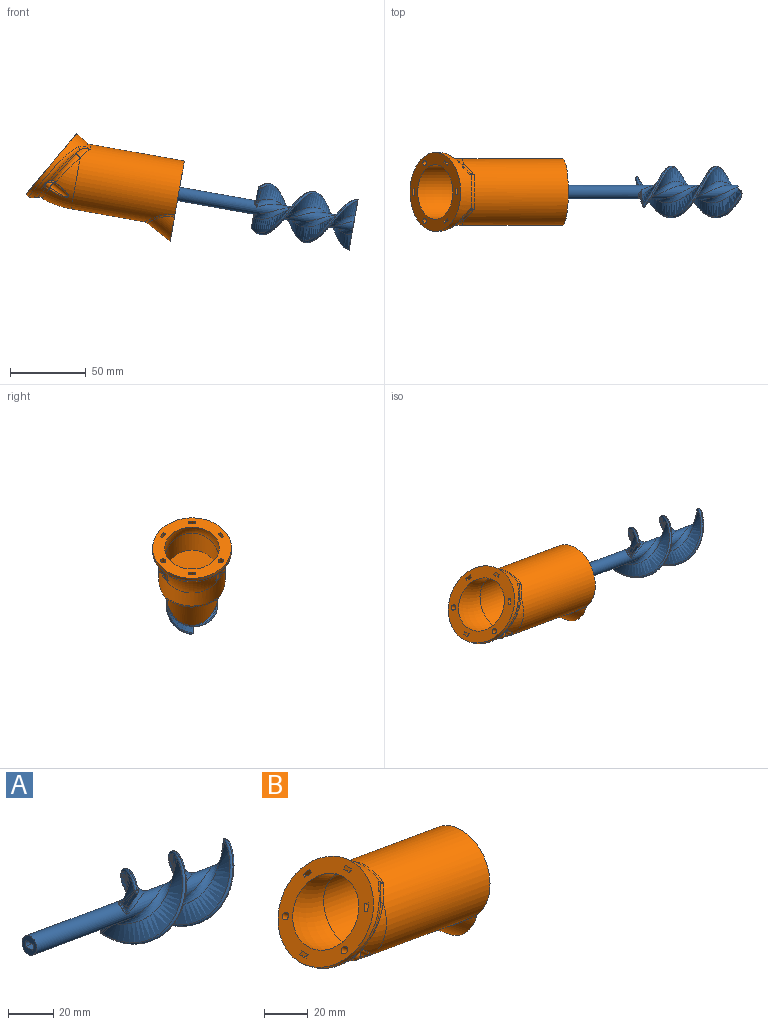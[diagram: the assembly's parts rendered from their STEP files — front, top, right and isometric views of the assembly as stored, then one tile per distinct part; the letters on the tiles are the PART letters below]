
ASSEMBLY  parts=2 mates=1
PART A: 48 faces, bbox 125.7x35.5x45.3 mm
  f0: bspline ~66.49x37.08mm, area 953.6mm2, adj f3,f20,f22,f23
  f1: bspline ~66.17x37.12mm, area 953.6mm2, adj f3,f19,f34,f35
  f2: plane 9.56x6.22mm, normal (-0.98,0,0.17), area 10.2mm2, adj f34,f36,f39,f41,f44,f45
  f3: plane 34.01x9.52mm, normal (0.98,0,-0.17), area 165.7mm2, adj f0,f1,f4,f5,f6,f7,f9,f11
  f4: bspline ~64.6x36.57mm, area 928.2mm2, adj f3,f18,f40,f44
  f5: bspline ~66.7x39.44mm, area 7mm2, adj f3,f35,f39,f40
  f6: bspline ~65.33x36.97mm, area 928.2mm2, adj f3,f21,f28,f32
  f7: bspline ~68.93x40.1mm, area 7mm2, adj f3,f23,f27,f28
  f8: plane 9.56x6.22mm, normal (-0.98,0,0.17), area 10.2mm2, adj f22,f24,f27,f29,f32,f33
  f9: cylinder r=4.5mm len=52.09mm, axis (0.98,0,-0.17), area 266.9mm2, adj f3,f10,f18,f20
  f10: cylinder r=4.5mm len=113.15mm, axis (0.98,0,-0.17), area 2007.6mm2, adj f9,f11,f12,f18,f19,f20,f21,f26
  f11: cylinder r=4.5mm len=22.25mm, axis (0.98,0,-0.17), area 89.1mm2, adj f3,f10,f19,f21
  f12: plane 9x8.86mm, normal (-0.98,0,0.17), area 49.6mm2, adj f10,f13,f14,f15,f16
  f13: plane 5.91x4mm, normal (-0.17,0,-0.98), area 24mm2, adj f12,f14,f16,f17
  f14: cylinder r=2.5mm len=6.43mm, axis (-0.98,0,0.17), area 19.3mm2, adj f12,f13,f15,f17
  f15: plane 5.91x4mm, normal (0.17,0,0.98), area 24mm2, adj f12,f14,f16,f17
  f16: cylinder r=2.5mm len=6.43mm, axis (-0.98,0,0.17), area 19.3mm2, adj f12,f13,f15,f17
  f17: plane 5x2.95mm, normal (-0.98,0,0.17), area 14mm2, adj f13,f14,f15,f16
  f18: bspline ~68.92x18.41mm, area 297.1mm2, adj f3,f4,f9,f10,f45
  f19: bspline ~70.5x19.33mm, area 299.9mm2, adj f1,f3,f10,f11,f36
  f20: bspline ~70.9x19.32mm, area 299.9mm2, adj f0,f3,f9,f10,f24
  f21: bspline ~69.05x19.32mm, area 297.1mm2, adj f3,f6,f10,f11,f33
  f22: bspline ~11.42x8.54mm, area 6.7mm2, adj f0,f8,f24,f25
  f23: bspline ~67.36x39.06mm, area 200.2mm2, adj f0,f3,f7,f25
  f24: bspline ~5.09x3.68mm, area 3.4mm2, adj f8,f20,f22,f26
  f25: sphere r=1mm, area 0.5mm2, adj f22,f23,f27
  f26: bspline ~3.52x1.96mm, area 1.9mm2, adj f10,f24,f29
  f27: bspline ~1.47x1.41mm, area 0.1mm2, adj f7,f8,f25,f30
  f28: bspline ~66.17x39.06mm, area 197.7mm2, adj f3,f6,f7,f30
  f29: torus R=5.5mm, axis (0.98,0,-0.17), area 2.8mm2, adj f8,f10,f26,f31
  f30: sphere r=1mm, area 1.5mm2, adj f27,f28,f32
  f31: bspline ~3.9x1.82mm, area 1.9mm2, adj f10,f29,f33
  f32: bspline ~12.63x9.51mm, area 22.6mm2, adj f6,f8,f30,f33
  f33: bspline ~6.38x2.81mm, area 5.7mm2, adj f8,f21,f31,f32
  f34: bspline ~11.46x8.54mm, area 6.7mm2, adj f1,f2,f36,f37
  f35: bspline ~66.3x39.14mm, area 200.2mm2, adj f1,f3,f5,f37
  f36: bspline ~5.09x3.82mm, area 3.4mm2, adj f2,f19,f34,f38
  f37: sphere r=1mm, area 0.7mm2, adj f34,f35,f39
  f38: bspline ~3.8x1.99mm, area 1.9mm2, adj f10,f36,f41
  f39: bspline ~1.58x1.47mm, area 0.1mm2, adj f2,f5,f37,f42
  f40: bspline ~65.33x38.94mm, area 197.7mm2, adj f3,f4,f5,f42
  f41: torus R=5.5mm, axis (0.98,0,-0.17), area 2.8mm2, adj f2,f10,f38,f43
  f42: sphere r=1mm, area 1.4mm2, adj f39,f40,f44
  f43: bspline ~3.32x2.46mm, area 1.9mm2, adj f10,f41,f45
  f44: bspline ~12.77x9.51mm, area 22.6mm2, adj f2,f4,f42,f45
  f45: bspline ~6.17x2.83mm, area 5.7mm2, adj f2,f18,f43,f44
  f46: cone r=0mm half-angle=59deg, axis (0.98,0,-0.17), area 1.3mm2, adj f47
  f47: cylinder r=0.6mm len=15.97mm, axis (0.98,0,-0.17), area 60.3mm2, adj f3,f46
PART B: 95 faces, bbox 123.3x72.3x89.8 mm
  f0: bspline ~21.17x20.89mm, area 78.8mm2, adj f1,f90,f91,f92,f93,f94
  f1: plane 6.16x5.23mm, normal (0.77,0,-0.64), area 19.3mm2, adj f0,f2,f84,f85,f87,f88,f89,f90
  f2: bspline ~2.61x1.99mm, area 2.3mm2, adj f1,f3,f84,f88
  f3: bspline ~4.22x3.01mm, area 3.2mm2, adj f2,f4,f83,f84
  f4: bspline ~3.88x3.69mm, area 3.3mm2, adj f3,f5,f6,f84
  f5: bspline ~4.67x2.25mm, area 3.2mm2, adj f4,f84,f93,f94
  f6: bspline ~52x33.72mm, area 400.3mm2, adj f4,f7,f79,f80,f81,f82,f83,f93
  f7: bspline ~3.69x3.56mm, area 3.3mm2, adj f6,f8,f77,f78
  f8: bspline ~4.22x3.01mm, area 3.2mm2, adj f7,f9,f78,f83
  f9: bspline ~2.97x2.27mm, area 2.3mm2, adj f8,f10,f78,f88
  f10: plane 6.16x5.23mm, normal (0.77,0,-0.64), area 19.3mm2, adj f9,f11,f12,f14,f15,f16,f76,f78
  f11: bspline ~2.77x1.84mm, area 2.1mm2, adj f10,f16,f77,f78
  f12: bspline ~2.37x2.15mm, area 0.7mm2, adj f10,f13,f14,f88
  f13: bspline ~15.13x11.52mm, area 24.5mm2, adj f12,f14,f15,f91
  f14: cylinder r=3mm len=13.01mm, axis (-0.77,0,0.64), area 62.7mm2, adj f10,f12,f13,f15
  f15: bspline ~2.57x2.06mm, area 1mm2, adj f10,f13,f14,f16
  f16: bspline ~21.52x21.22mm, area 78.8mm2, adj f10,f11,f15,f17,f79,f91
  f17: bspline ~11.35x10.37mm, area 31.2mm2, adj f16,f18,f21,f79,f80
  f18: bspline ~2.84x1.97mm, area 0.9mm2, adj f17,f19,f80
  f19: bspline ~27.31x5.39mm, area 48.2mm2, adj f18,f20,f21,f81
  f20: bspline ~2.84x1.97mm, area 0.9mm2, adj f19,f82,f92
  f21: cylinder r=22mm len=74.61mm, axis (-0.98,0,0.17), area 8639.8mm2, adj f17,f19,f22,f24,f91,f92
  f22: bspline ~34.5x21.07mm, area 105.4mm2, adj f21,f23,f24
  f23: extruded ~32.71x11.03mm, area 0mm2, adj f22,f24
  f24: plane 71.91x62.94mm, normal (0.98,0,-0.17), area 1281.1mm2, adj f21,f22,f23,f25,f66,f67,f68,f69
  f25: cylinder r=0.75mm len=4.2mm, axis (-0.98,0,0.17), area 18.8mm2, adj f24,f26
  f26: plane 36x27.12mm, normal (-0.98,0,0.17), area 673.3mm2, adj f25,f27,f28,f33,f37,f60,f65
  f27: torus R=19.9mm, axis (0.98,0,-0.17), area 98.8mm2, adj f26,f28,f65,f73
  f28: bspline ~3.69x3.37mm, area 3.5mm2, adj f26,f27,f29,f33
  f29: bspline ~3.84x2.38mm, area 0mm2, adj f28,f30,f73
  f30: sphere r=4mm, area 0.7mm2, adj f29,f31,f33,f69
  f31: bspline ~3.46x3.43mm, area 3.5mm2, adj f30,f32,f72,f73
  f32: bspline ~2.98x2.88mm, area 0.1mm2, adj f31,f69,f71
  f33: torus R=5.96mm, axis (0.98,0,-0.17), area 4.9mm2, adj f26,f28,f30,f34,f37,f68,f69
  f34: bspline ~3.23x2.15mm, area 1.3mm2, adj f33,f35,f37,f68
  f35: bspline ~29.02x16.13mm, area 79.3mm2, adj f34,f36,f37,f68
  f36: bspline ~3.23x2.15mm, area 1.3mm2, adj f35,f37,f60,f68
  f37: cylinder r=18mm len=69.61mm, axis (-0.98,0,0.17), area 6879.1mm2, adj f26,f33,f34,f35,f36,f38,f60
  f38: torus R=36mm, axis (0,-1,0), area 2131.8mm2, adj f37,f39
  f39: plane 52x39.83mm, normal (-0.77,0,0.64), area 1054.6mm2, adj f38,f40,f42,f43,f44,f45,f47,f48
  f40: plane 4.47x3.98mm, normal (0.56,0.5,0.66), area 10mm2, adj f39,f41,f42,f44
  f41: plane 3.73x3.42mm, normal (-0.77,0,0.64), area 8mm2, adj f40,f42,f43,f44
  f42: plane 6.06x5.87mm, normal (-0.32,0.87,-0.38), area 20mm2, adj f39,f40,f41,f43
  f43: plane 4.47x3.98mm, normal (-0.56,-0.5,-0.66), area 10mm2, adj f39,f41,f42,f44
  f44: plane 6.06x5.87mm, normal (0.32,-0.87,0.38), area 20mm2, adj f39,f40,f41,f43
  f45: plane 4.47x3.98mm, normal (-0.56,0.5,-0.66), area 10mm2, adj f39,f46,f47,f49
  f46: plane 3.73x3.42mm, normal (-0.77,0,0.64), area 8mm2, adj f45,f47,f48,f49
  f47: plane 6.06x5.87mm, normal (-0.32,-0.87,-0.38), area 20mm2, adj f39,f45,f46,f48
  f48: plane 4.47x3.98mm, normal (0.56,-0.5,0.66), area 10mm2, adj f39,f46,f47,f49
  f49: plane 6.06x5.87mm, normal (0.32,0.87,0.38), area 20mm2, adj f39,f45,f46,f48
  f50: plane 5.12x4.75mm, normal (0,1,0), area 10mm2, adj f39,f51,f52,f54
  f51: plane 4x1.53mm, normal (-0.77,0,0.64), area 8mm2, adj f50,f52,f53,f54
  f52: plane 4x3.83mm, normal (-0.64,0,-0.77), area 20mm2, adj f39,f50,f51,f53
  f53: plane 5.12x4.75mm, normal (0,-1,0), area 10mm2, adj f39,f51,f52,f54
  f54: plane 4x3.83mm, normal (0.64,0,0.77), area 20mm2, adj f39,f50,f51,f53
  f55: plane 4x3.83mm, normal (-0.64,0,-0.77), area 20mm2, adj f39,f56,f57,f59
  f56: plane 4x1.53mm, normal (-0.77,0,0.64), area 8mm2, adj f55,f57,f58,f59
  f57: plane 5.12x4.75mm, normal (0,-1,0), area 10mm2, adj f39,f55,f56,f58
  f58: plane 4x3.83mm, normal (0.64,0,0.77), area 20mm2, adj f39,f56,f57,f59
  f59: plane 5.12x4.75mm, normal (0,1,0), area 10mm2, adj f39,f55,f56,f58
  f60: torus R=5.96mm, axis (0.98,0,-0.17), area 4.9mm2, adj f26,f36,f37,f61,f65,f67,f68
  f61: sphere r=4mm, area 0.7mm2, adj f60,f62,f64,f67
  f62: bspline ~3.57x3.48mm, area 3.5mm2, adj f61,f63,f73,f74
  f63: bspline ~2.98x2.88mm, area 0.1mm2, adj f62,f67,f75
  f64: bspline ~3.84x2.38mm, area 0mm2, adj f61,f65,f73
  f65: bspline ~3.69x3.37mm, area 3.5mm2, adj f26,f27,f60,f64
  f66: plane 0.48x0.35mm, normal (0,1,0), area 0.1mm2, adj f24,f67,f75
  f67: cylinder r=4mm len=2.29mm, axis (0.78,0,-0.62), area 1.8mm2, adj f24,f60,f61,f63,f66,f68
  f68: extruded ~28.06x22.68mm, area 553.6mm2, adj f24,f33,f34,f35,f36,f60,f67,f69
  f69: cylinder r=4mm len=2.29mm, axis (0.78,0,-0.62), area 1.8mm2, adj f24,f30,f32,f33,f68,f70
  f70: plane 0.48x0.35mm, normal (0,-1,0), area 0.1mm2, adj f24,f69,f71
  f71: cylinder r=4mm len=0.53mm, axis (-0.98,0,0.17), area 0.1mm2, adj f24,f32,f70,f72
  f72: bspline ~3.33x2.67mm, area 1.9mm2, adj f24,f31,f71,f73
  f73: sphere r=18mm, area 51.5mm2, adj f24,f27,f29,f31,f62,f64,f72,f74
  f74: bspline ~3.33x2.67mm, area 1.9mm2, adj f24,f62,f73,f75
  f75: cylinder r=4mm len=0.53mm, axis (-0.98,0,0.17), area 0.1mm2, adj f24,f63,f66,f74
  f76: cylinder r=1.75mm len=9.14mm, axis (-0.77,0,0.64), area 99mm2, adj f10,f39
  f77: bspline ~4.15x2.24mm, area 3.2mm2, adj f7,f11,f78,f79
  f78: cylinder r=3mm len=6.4mm, axis (0.77,0,-0.64), area 20.5mm2, adj f7,f8,f9,f10,f11,f77
  f79: bspline ~29.75x27.58mm, area 39.4mm2, adj f6,f16,f17,f77
  f80: bspline ~7.86x7.28mm, area 15mm2, adj f6,f17,f18,f81
  f81: cylinder r=26mm len=52mm, axis (0.77,0,-0.64), area 760.3mm2, adj f6,f19,f39,f80,f82
  f82: bspline ~6.82x6.16mm, area 15mm2, adj f6,f20,f81,f92
  f83: bspline ~47.13x14.03mm, area 113mm2, adj f3,f6,f8,f88
  f84: cylinder r=3mm len=6.4mm, axis (0.77,0,-0.64), area 20.5mm2, adj f1,f2,f3,f4,f5,f94
  f85: cylinder r=3mm len=13.01mm, axis (-0.77,0,0.64), area 62.7mm2, adj f1,f86,f87,f90
  f86: bspline ~15.13x11.52mm, area 24.5mm2, adj f85,f87,f90,f91
  f87: bspline ~1.72x1.7mm, area 0.7mm2, adj f1,f85,f86,f88
  f88: bspline ~36.77x8.45mm, area 106.4mm2, adj f1,f2,f9,f10,f12,f83,f87,f91
  f89: cylinder r=1.75mm len=9.14mm, axis (-0.77,0,0.64), area 99mm2, adj f1,f39
  f90: bspline ~2.48x2.02mm, area 1mm2, adj f0,f1,f85,f86
  f91: torus R=36mm, axis (0,-1,0), area 1043.4mm2, adj f0,f13,f16,f21,f86,f88
  f92: bspline ~11.46x10.06mm, area 31.2mm2, adj f0,f20,f21,f82,f93
  f93: bspline ~29.69x27.54mm, area 39.4mm2, adj f0,f5,f6,f92
  f94: bspline ~2.86x1.86mm, area 2.1mm2, adj f0,f1,f5,f84
PLACE A rot(axis=(0.98,0,-0.17),4.1deg) t=(28.06,-3.12,71.42)mm
PLACE B t=(-91.2,-0.03,92.56)mm
MATE cylindrical A.f9 <-> B.f25  axis (0.98,0,-0.17) through (120.86,-0.03,10.96)mm
